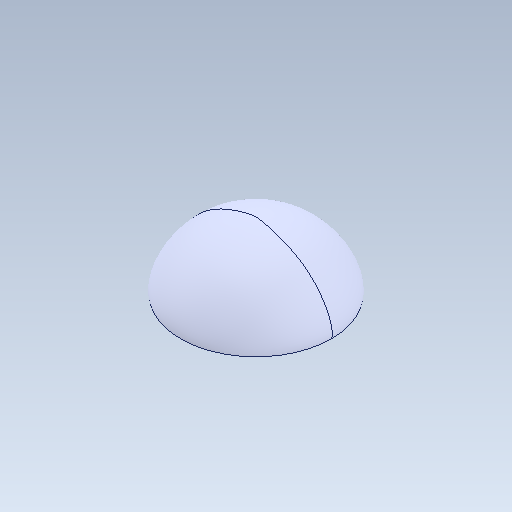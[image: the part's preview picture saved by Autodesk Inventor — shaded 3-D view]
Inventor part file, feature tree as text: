
AUTODESK INVENTOR PART (.ipt)
format: ipt  version: 2020.1 (Build 241239000, 239)  size: 123,904 bytes
history: native  units: mm
features: revolve x1
ambient origin geometry x8: Origin, YZ Plane, XZ Plane, XY Plane, X Axis, Y Axis, Z Axis, Center Point
bodies: Solid1 (feature_tree)
feature tree (1):
  revolve  "Revolve1"  [1 undecoded]
note: 1 required parameter value undecoded (feature->parameter linkage not recoverable at this tier; creation-order binding heuristic only, values carry confidence <= 0.55)
